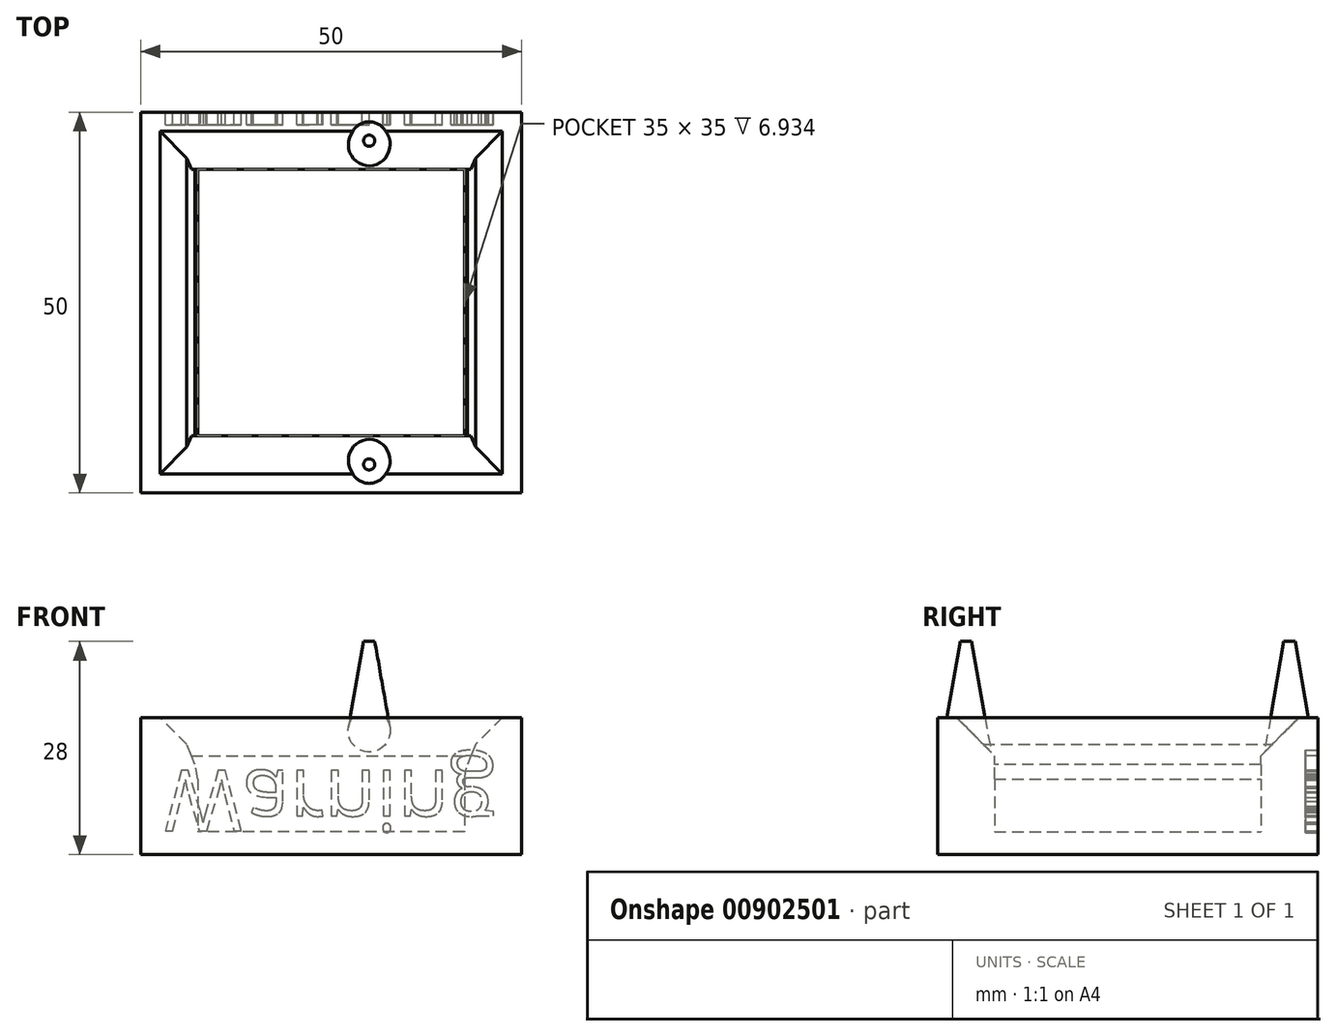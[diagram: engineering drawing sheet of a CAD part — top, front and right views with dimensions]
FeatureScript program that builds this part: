
annotation { "Feature Type Name" : "Feature", "Feature Type Description" : "" }
export const myFeature = defineFeature(function(context is Context, id is Id, definition is map)
    precondition{}
    {
        {
            assignVariable(context, id + "F0", {"name" : "d", "anyValue" : 5});
        }
        {
            var Q0;
            Q0=qCreatedBy(makeId("Top.planeOp"),FACE);
            var sketch = newSketch(context, id + "F1", { "sketchPlane" : qUnion([Q0])});
            skLineSegment(sketch, "E0.bottom", {"start": v(0, 0) * mm, "end": v(-50, 0) * mm});
            skLineSegment(sketch, "E0.top", {"start": v(0, 50) * mm, "end": v(-50, 50) * mm});
            skLineSegment(sketch, "E0.left", {"start": v(0, 0) * mm, "end": v(0, 50) * mm});
            skLineSegment(sketch, "E0.right", {"start": v(-50, 0) * mm, "end": v(-50, 50) * mm});
            skLineSegment(sketch, "E1.bottom", {"start": v(-7.5, 7.5) * mm, "end": v(-42.5, 7.5) * mm});
            skLineSegment(sketch, "E1.top", {"start": v(-7.5, 42.5) * mm, "end": v(-42.5, 42.5) * mm});
            skLineSegment(sketch, "E1.left", {"start": v(-7.5, 7.5) * mm, "end": v(-7.5, 42.5) * mm});
            skLineSegment(sketch, "E1.right", {"start": v(-42.5, 7.5) * mm, "end": v(-42.5, 42.5) * mm});
            skSolve(sketch);
        }
        {
            var Q0;
            Q0 = qSketchRegion(id + "F1", true);
            extrude(context, id + "F2", {"entities" : qUnion([Q0]), "depth" : 15 * mm, "offsetDistance" : 25 * mm});
        }
        {
            var Q0;
            Q0=makeQuery(id+"F1.imprint","IMPRINT",FACE,{"disambiguationData":[TD([[makeQuery(id+"F1.imprint","IMPRINT",EDGE,{"derivedFrom":sQuery(id+"F1.wireOp",EDGE,"E1.bottom")}),-1.0]])]});
            var Q1;
            Q1=makeQuery(id+"F1.imprint","IMPRINT",FACE,{"disambiguationData":[TD([[makeQuery(id+"F1.imprint","IMPRINT",EDGE,{"derivedFrom":sQuery(id+"F1.wireOp",EDGE,"E0.bottom")}),-1.0]])]});
            extrude(context, id + "F3", {"entities" : qUnion([Q0, Q1]), "operationType" : NewBodyOperationType.ADD, "oppositeDirection" : true, "depth" : 3 * mm, "offsetDistance" : 25 * mm});
        }
        {
            var Q0;
            Q0=makeQuery(id+"F2.opExtrude","CAP_FACE",FACE,{"disambiguationData":[OSD([sQuery(id+"F1.wireOp",EDGE,"E0.bottom"),sQuery(id+"F1.wireOp",EDGE,"E0.top"),sQuery(id+"F1.wireOp",EDGE,"E0.left"),sQuery(id+"F1.wireOp",EDGE,"E0.right"),sQuery(id+"F1.wireOp",EDGE,"E1.bottom"),sQuery(id+"F1.wireOp",EDGE,"E1.top"),sQuery(id+"F1.wireOp",EDGE,"E1.left"),sQuery(id+"F1.wireOp",EDGE,"E1.right")])],"isStart":false});
            var sketch = newSketch(context, id + "F4", { "sketchPlane" : qUnion([Q0])});
            skCircle(sketch, "E2", {"center": v(-20, 46.25) * mm, "radius": 2.5 * mm});
            skCircle(sketch, "E3", {"center": v(-20, 3.75) * mm, "radius": 2.5 * mm});
            skSolve(sketch);
        }
        {
            var Q0;
            Q0=makeQuery(id+"F4.imprint","IMPRINT",FACE,{"disambiguationData":[TD([[makeQuery(id+"F4.imprint","IMPRINT",EDGE,{"derivedFrom":sQuery(id+"F4.wireOp",EDGE,"E2")}),1.0]])]});
            var Q1;
            Q1=makeQuery(id+"F4.imprint","IMPRINT",FACE,{"disambiguationData":[TD([[makeQuery(id+"F4.imprint","IMPRINT",EDGE,{"derivedFrom":sQuery(id+"F4.wireOp",EDGE,"E3")}),1.0]])]});
            extrude(context, id + "F5", {"entities" : qUnion([Q0, Q1]), "operationType" : NewBodyOperationType.ADD, "depth" : 10 * mm, "offsetDistance" : 25 * mm, "hasDraft" : true, "draftAngle" : 10 * degree, "draftPullDirection" : true});
        }
        {
            var Q0;
            Q0=makeQuery(id+"F2.opExtrude","CAP_EDGE",EDGE,{"disambiguationData":[OSD([sQuery(id+"F1.wireOp",EDGE,"E1.right")])],"isStart":false});
            var Q1;
            Q1=makeQuery(id+"F2.opExtrude","CAP_EDGE",EDGE,{"disambiguationData":[OSD([sQuery(id+"F1.wireOp",EDGE,"E1.top")])],"isStart":false});
            var Q2;
            Q2=makeQuery(id+"F2.opExtrude","CAP_EDGE",EDGE,{"disambiguationData":[OSD([sQuery(id+"F1.wireOp",EDGE,"E1.left")])],"isStart":false});
            var Q3;
            Q3=makeQuery(id+"F2.opExtrude","CAP_EDGE",EDGE,{"disambiguationData":[OSD([sQuery(id+"F1.wireOp",EDGE,"E1.bottom")])],"isStart":false});
            chamfer(context, id + "F6", {"entities" : qUnion([Q0, Q1, Q2, Q3]), "width" : 5 * mm, "tangentPropagation" : true});
        }
        {
            var Q0;
            {var subQ0=sQuery(id+"F1.wireOp",EDGE,"E1.right");Q0=makeQuery(id+"F6.opChamfer","BLEND_EDGE",EDGE,{"blendedFrom":[makeQuery(id+"F2.opExtrude","CAP_EDGE",EDGE,{"disambiguationData":[OSD([subQ0])],"isStart":false}),makeQuery(id+"F2.opExtrude","SWEPT_FACE",FACE,{"disambiguationData":[OSD([subQ0])]})],"blendedInto":[makeQuery(id+"F2.opExtrude","SWEPT_FACE",FACE,{"disambiguationData":[OSD([subQ0])]})]});}
            var Q1;
            {var subQ0=sQuery(id+"F1.wireOp",EDGE,"E1.left");Q1=makeQuery(id+"F6.opChamfer","BLEND_EDGE",EDGE,{"blendedFrom":[makeQuery(id+"F2.opExtrude","CAP_EDGE",EDGE,{"disambiguationData":[OSD([subQ0])],"isStart":false}),makeQuery(id+"F2.opExtrude","SWEPT_FACE",FACE,{"disambiguationData":[OSD([subQ0])]})],"blendedInto":[makeQuery(id+"F2.opExtrude","SWEPT_FACE",FACE,{"disambiguationData":[OSD([subQ0])]})]});}
            chamfer(context, id + "F7", {"entities" : qUnion([Q0, Q1]), "width" : 5 * mm, "tangentPropagation" : true});
        }
        {
            var Q0;
            {var subQ0=sQuery(id+"F1.wireOp",EDGE,"E1.right");var subQ1=makeQuery(id+"F2.opExtrude","SWEPT_FACE",FACE,{"disambiguationData":[OSD([subQ0])]});Q0=makeQuery(id+"F7.opChamfer","BLEND_EDGE",EDGE,{"blendedFrom":[makeQuery(id+"F6.opChamfer","BLEND_EDGE",EDGE,{"blendedFrom":[makeQuery(id+"F2.opExtrude","CAP_EDGE",EDGE,{"disambiguationData":[OSD([subQ0])],"isStart":false}),subQ1],"blendedInto":[subQ1]}),subQ1],"blendedInto":[subQ1]});}
            var Q1;
            {var subQ0=sQuery(id+"F1.wireOp",EDGE,"E1.left");var subQ1=makeQuery(id+"F2.opExtrude","SWEPT_FACE",FACE,{"disambiguationData":[OSD([subQ0])]});Q1=makeQuery(id+"F7.opChamfer","BLEND_EDGE",EDGE,{"blendedFrom":[makeQuery(id+"F6.opChamfer","BLEND_EDGE",EDGE,{"blendedFrom":[makeQuery(id+"F2.opExtrude","CAP_EDGE",EDGE,{"disambiguationData":[OSD([subQ0])],"isStart":false}),subQ1],"blendedInto":[subQ1]}),subQ1],"blendedInto":[subQ1]});}
            chamfer(context, id + "F8", {"entities" : qUnion([Q0, Q1]), "width" : 5 * mm, "tangentPropagation" : true});
        }
        {
            var Q0;
            {var subQ0=sQuery(id+"F1.wireOp",EDGE,"E0.top");Q0=makeQuery(id+"F3.boolean.opBoolean","MERGE",FACE,{"derivedFrom":[makeQuery(id+"F2.opExtrude","SWEPT_FACE",FACE,{"disambiguationData":[OSD([subQ0])]}),makeQuery(id+"F3.opExtrude","SWEPT_FACE",FACE,{"disambiguationData":[OSD([subQ0])]})]});}
            var sketch = newSketch(context, id + "F9", { "sketchPlane" : qUnion([Q0])});
            skText(sketch, "E4", { "text": "Warning", "fontName": "OpenSans-Regular.ttf"});
            const initialGuessF9  = {"E4": [0.04693, 0.00805, -1, 0, 0.008]};
            skSetInitialGuess(sketch, initialGuessF9);
            skSolve(sketch);
        }
        {
            var Q0;
            Q0 = qSketchRegion(id + "F9", true);
            extrude(context, id + "F10", {"entities" : qUnion([Q0]), "operationType" : NewBodyOperationType.REMOVE, "oppositeDirection" : true, "depth" : (getVariable(context, 'd') / 3) * mm, "offsetDistance" : 25 * mm});
        }
    });
